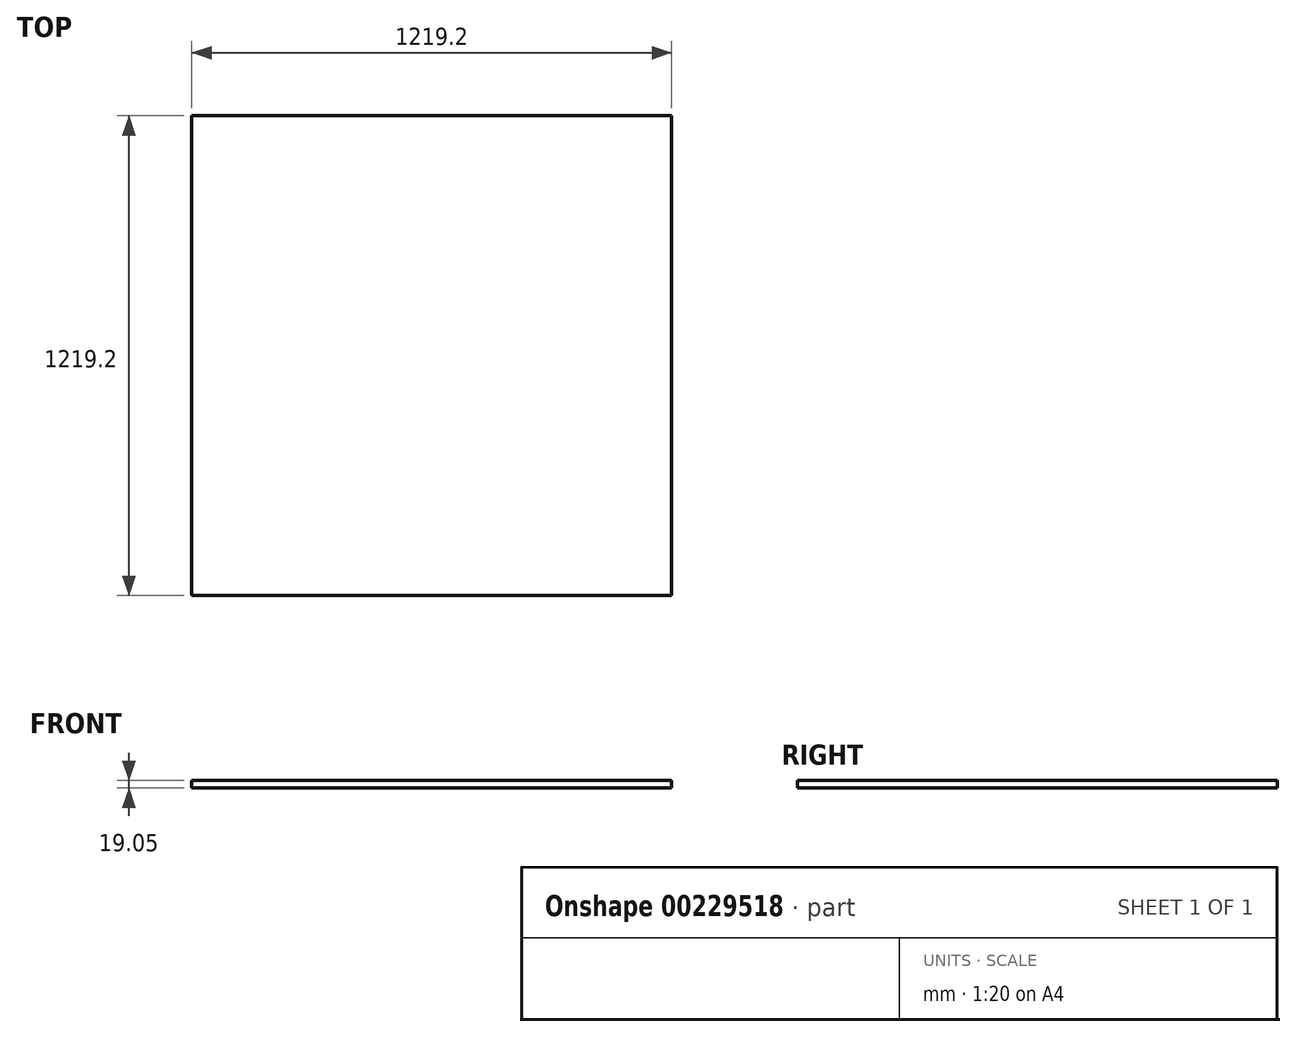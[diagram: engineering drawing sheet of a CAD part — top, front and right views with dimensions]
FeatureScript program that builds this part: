
annotation { "Feature Type Name" : "Feature", "Feature Type Description" : "" }
export const myFeature = defineFeature(function(context is Context, id is Id, definition is map)
    precondition{}
    {
        {
            var Q0;
            Q0=qCreatedBy(makeId("Top.planeOp"),FACE);
            var sketch = newSketch(context, id + "F0", { "sketchPlane" : qUnion([Q0])});
            skLineSegment(sketch, "E0.bottom", {"start": v(0, 0) * mm, "end": v(1219.2, 0) * mm});
            skLineSegment(sketch, "E0.top", {"start": v(0, -1219.2) * mm, "end": v(1219.2, -1219.2) * mm});
            skLineSegment(sketch, "E0.left", {"start": v(0, 0) * mm, "end": v(0, -1219.2) * mm});
            skLineSegment(sketch, "E0.right", {"start": v(1219.2, 0) * mm, "end": v(1219.2, -1219.2) * mm});
            skSolve(sketch);
        }
        {
            var Q0;
            Q0=makeQuery(id+"F0.imprint","IMPRINT",FACE,{"disambiguationData":[TD([[makeQuery(id+"F0.imprint","IMPRINT",EDGE,{"derivedFrom":sQuery(id+"F0.wireOp",EDGE,"E0.bottom")}),-1.0]])]});
            extrude(context, id + "F1", {"entities" : qUnion([Q0]), "depth" : 19.05 * mm});
        }
    });
